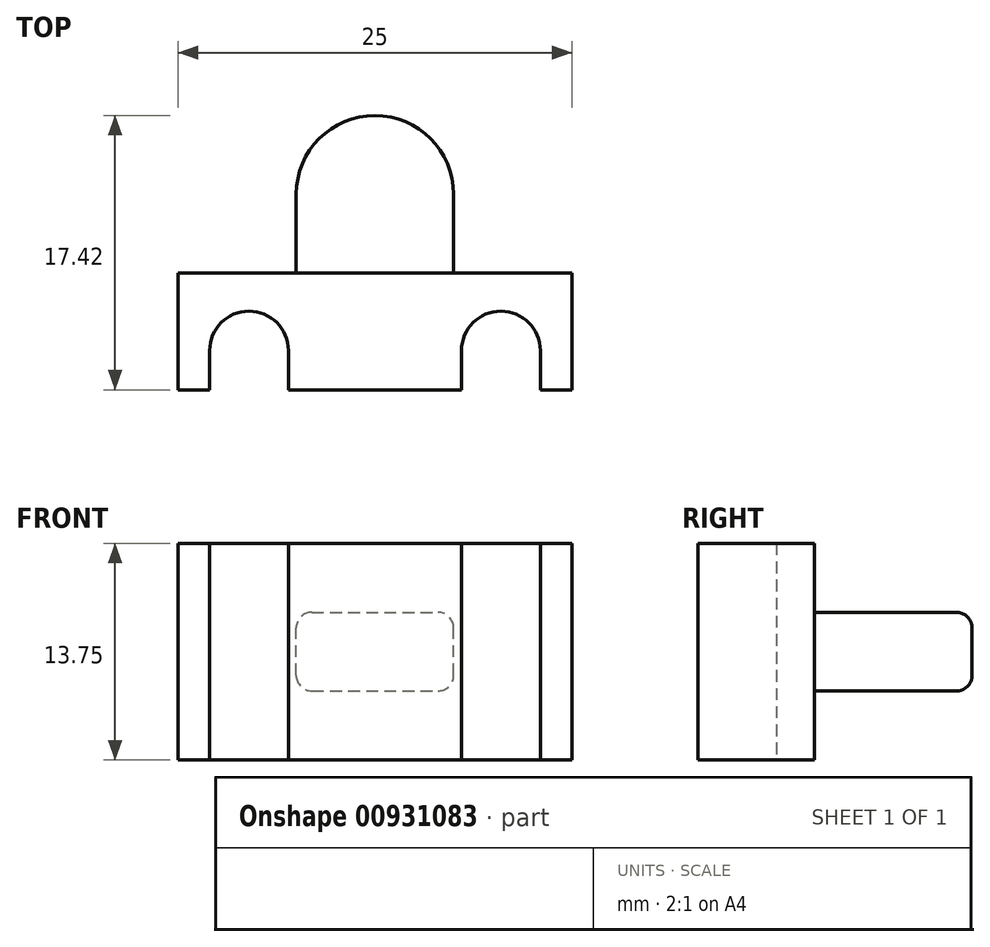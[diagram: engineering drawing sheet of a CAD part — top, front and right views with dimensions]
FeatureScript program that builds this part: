
annotation { "Feature Type Name" : "Feature", "Feature Type Description" : "" }
export const myFeature = defineFeature(function(context is Context, id is Id, definition is map)
    precondition{}
    {
        {
            var Q0;
            Q0=qCreatedBy(makeId("Top.planeOp"),FACE);
            var sketch = newSketch(context, id + "F0", { "sketchPlane" : qUnion([Q0])});
            skLineSegment(sketch, "E0.left", {"start": v(-17.07, -2.9) * mm, "end": v(-17.07, -7.82) * mm});
            skLineSegment(sketch, "E0.right", {"start": v(7.93, -2.9) * mm, "end": v(7.93, -7.82) * mm});
            skArc(sketch, "E1", {"start": v(-10.07, -7.82) * mm, "mid": v(-12.57, -5.32) * mm, "end": v(-15.07, -7.82) * mm});
            skArc(sketch, "E2", {"start": v(5.93, -7.82) * mm, "mid": v(3.43, -5.32) * mm, "end": v(0.93, -7.82) * mm});
            skLineSegment(sketch, "E3", {"start": v(5.93, -7.82) * mm, "end": v(5.93, -10.32) * mm});
            skLineSegment(sketch, "E4", {"start": v(5.93, -10.32) * mm, "end": v(7.93, -10.32) * mm});
            skLineSegment(sketch, "E5", {"start": v(7.93, -10.32) * mm, "end": v(7.93, -7.82) * mm});
            skLineSegment(sketch, "E6", {"start": v(-15.07, -7.82) * mm, "end": v(-15.07, -10.32) * mm});
            skLineSegment(sketch, "E7", {"start": v(-15.07, -10.32) * mm, "end": v(-17.07, -10.32) * mm});
            skLineSegment(sketch, "E8", {"start": v(-17.07, -10.32) * mm, "end": v(-17.07, -7.82) * mm});
            skLineSegment(sketch, "E9", {"start": v(-10.07, -7.82) * mm, "end": v(-10.07, -10.32) * mm});
            skLineSegment(sketch, "E10", {"start": v(0.93, -7.82) * mm, "end": v(0.93, -10.32) * mm});
            skLineSegment(sketch, "E11", {"start": v(0.93, -10.32) * mm, "end": v(-10.07, -10.32) * mm});
            skLineSegment(sketch, "E12", {"start": v(-17.07, -2.9) * mm, "end": v(7.93, -2.9) * mm});
            skSolve(sketch);
        }
        {
            var Q0;
            Q0=makeQuery(id+"F0.imprint","IMPRINT",FACE,{"disambiguationData":[TD([[makeQuery(id+"F0.imprint","IMPRINT",EDGE,{"derivedFrom":sQuery(id+"F0.wireOp",EDGE,"E0.left")}),1.0]])]});
            extrude(context, id + "F1", {"entities" : qUnion([Q0]), "depth" : 13.75 * mm, "offsetDistance" : 25 * mm});
        }
        {
            var Q0;
            Q0=makeQuery(id+"F1.opExtrude","SWEPT_FACE",FACE,{"disambiguationData":[OSD([sQuery(id+"F0.wireOp",EDGE,"E12")])]});
            var sketch = newSketch(context, id + "F2", { "sketchPlane" : qUnion([Q0])});
            skLineSegment(sketch, "E13.bottom", {"start": v(9.57, 4.38) * mm, "end": v(-0.43, 4.38) * mm});
            skLineSegment(sketch, "E13.top", {"start": v(9.57, 9.38) * mm, "end": v(-0.43, 9.38) * mm});
            skLineSegment(sketch, "E13.left", {"start": v(9.57, 4.38) * mm, "end": v(9.57, 9.38) * mm});
            skLineSegment(sketch, "E13.right", {"start": v(-0.43, 4.38) * mm, "end": v(-0.43, 9.38) * mm});
            skSolve(sketch);
        }
        {
            var Q0;
            Q0=makeQuery(id+"F2.imprint","IMPRINT",FACE,{"disambiguationData":[TD([[makeQuery(id+"F2.imprint","IMPRINT",EDGE,{"derivedFrom":sQuery(id+"F2.wireOp",EDGE,"E13.bottom")}),-1.0]])]});
            extrude(context, id + "F3", {"entities" : qUnion([Q0]), "operationType" : NewBodyOperationType.ADD, "depth" : 10 * mm, "offsetDistance" : 25 * mm});
        }
        {
            var Q0;
            Q0=makeQuery(id+"F3.opExtrude","CAP_EDGE",EDGE,{"disambiguationData":[OSD([sQuery(id+"F2.wireOp",EDGE,"E13.top")])],"isStart":false});
            var Q1;
            Q1=makeQuery(id+"F3.opExtrude","CAP_EDGE",EDGE,{"disambiguationData":[OSD([sQuery(id+"F2.wireOp",EDGE,"E13.bottom")])],"isStart":false});
            var Q2;
            Q2=makeQuery(id+"F3.opExtrude","SWEPT_EDGE",EDGE,{"disambiguationData":[OSD([sQuery(id+"F2.wireOp",EDGE,"E13.bottom"),sQuery(id+"F2.wireOp",EDGE,"E13.left")])]});
            var Q3;
            Q3=makeQuery(id+"F3.opExtrude","SWEPT_EDGE",EDGE,{"disambiguationData":[OSD([sQuery(id+"F2.wireOp",EDGE,"E13.top"),sQuery(id+"F2.wireOp",EDGE,"E13.left")])]});
            var Q4;
            Q4=makeQuery(id+"F3.opExtrude","SWEPT_EDGE",EDGE,{"disambiguationData":[OSD([sQuery(id+"F2.wireOp",EDGE,"E13.top"),sQuery(id+"F2.wireOp",EDGE,"E13.right")])]});
            var Q5;
            Q5=makeQuery(id+"F3.opExtrude","SWEPT_EDGE",EDGE,{"disambiguationData":[OSD([sQuery(id+"F2.wireOp",EDGE,"E13.bottom"),sQuery(id+"F2.wireOp",EDGE,"E13.right")])]});
            fillet(context, id + "F4", {"entities" : qUnion([Q0, Q1, Q2, Q3, Q4, Q5]), "radius" : 1 * mm, "tangentPropagation" : true, "allowEdgeOverflow" : false});
        }
        {
            var Q0;
            Q0=makeQuery(id+"F3.opExtrude","CAP_EDGE",EDGE,{"disambiguationData":[OSD([sQuery(id+"F2.wireOp",EDGE,"E13.left")])],"isStart":false});
            var Q1;
            Q1=makeQuery(id+"F3.opExtrude","CAP_EDGE",EDGE,{"disambiguationData":[OSD([sQuery(id+"F2.wireOp",EDGE,"E13.right")])],"isStart":false});
            fillet(context, id + "F5", {"entities" : qUnion([Q0, Q1]), "radius" : 5 * mm, "tangentPropagation" : true, "allowEdgeOverflow" : false});
        }
    });
